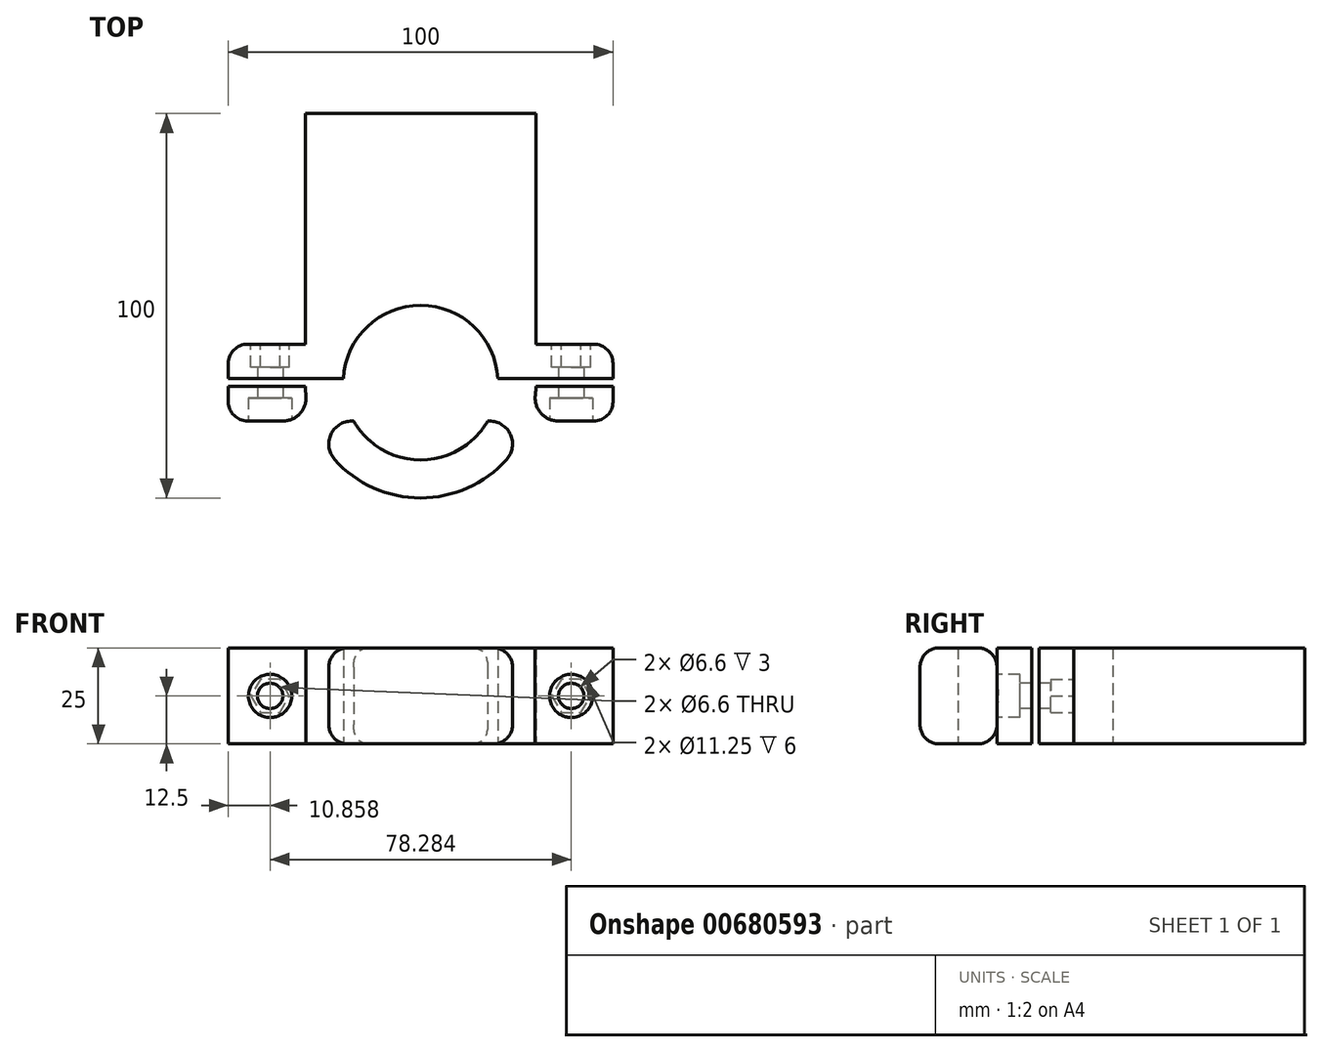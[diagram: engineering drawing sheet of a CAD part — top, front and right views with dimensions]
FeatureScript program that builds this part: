
annotation { "Feature Type Name" : "Feature", "Feature Type Description" : "" }
export const myFeature = defineFeature(function(context is Context, id is Id, definition is map)
    precondition{}
    {
        {
            var Q0;
            Q0=qCreatedBy(makeId("Top.planeOp"),FACE);
            var sketch = newSketch(context, id + "F0", { "sketchPlane" : qUnion([Q0])});
            skCircle(sketch, "E0", {"center": v(0, 0) * mm, "radius": 20.1 * mm});
            skLineSegment(sketch, "E1.bottom", {"start": v(-50, 10) * mm, "end": v(50, 10) * mm});
            skLineSegment(sketch, "E1.top", {"start": v(-50, -10) * mm, "end": v(50, -10) * mm});
            skLineSegment(sketch, "E1.left", {"start": v(-50, 10) * mm, "end": v(-50, -10) * mm});
            skLineSegment(sketch, "E1.right", {"start": v(50, 10) * mm, "end": v(50, -10) * mm});
            skLineSegment(sketch, "E2.bottom", {"start": v(-30, 0) * mm, "end": v(30, 0) * mm});
            skLineSegment(sketch, "E2.top", {"start": v(-30, 70) * mm, "end": v(30, 70) * mm});
            skLineSegment(sketch, "E2.left", {"start": v(-30, 0) * mm, "end": v(-30, 70) * mm});
            skLineSegment(sketch, "E2.right", {"start": v(30, 0) * mm, "end": v(30, 70) * mm});
            skCircle(sketch, "E3", {"center": v(0, 0) * mm, "radius": 30 * mm});
            skSolve(sketch);
        }
        {
            var Q0;
            {var subQ1=sQuery(id+"F0.wireOp",EDGE,"E2.top");Q0=makeQuery(id+"F0.imprint","IMPRINT",FACE,{"disambiguationData":[TD([[makeQuery(id+"F0.imprint","IMPRINT",EDGE,{"derivedFrom":subQ1}),-1.0]])]});}
            var Q1;
            {var subQ5=sQuery(id+"F0.wireOp",EDGE,"E1.right");Q1=makeQuery(id+"F0.imprint","IMPRINT",FACE,{"disambiguationData":[TD([[makeQuery(id+"F0.imprint","IMPRINT",EDGE,{"derivedFrom":subQ5}),-1.0]])]});}
            var Q2;
            {var subQ0=sQuery(id+"F0.wireOp",EDGE,"E1.bottom");var subQ1=sQuery(id+"F0.wireOp",EDGE,"E0");var subQ2=makeQuery(id+"F0.imprint","INTERSECT",VERTEX,{"disambiguationData":[OD(0.0)],"derivedFrom":[subQ1,subQ0]});Q2=makeQuery(id+"F0.imprint","IMPRINT",FACE,{"disambiguationData":[TD([[makeQuery(id+"F0.imprint","IMPRINT",EDGE,{"disambiguationData":[TD([[subQ2,-1.0]])],"derivedFrom":subQ1}),-1.0]])]});}
            var Q3;
            {var subQ0=sQuery(id+"F0.wireOp",EDGE,"E1.bottom");var subQ1=sQuery(id+"F0.wireOp",EDGE,"E0");var subQ2=makeQuery(id+"F0.imprint","INTERSECT",VERTEX,{"disambiguationData":[OD(1.0)],"derivedFrom":[subQ1,subQ0]});Q3=makeQuery(id+"F0.imprint","IMPRINT",FACE,{"disambiguationData":[TD([[makeQuery(id+"F0.imprint","IMPRINT",EDGE,{"disambiguationData":[TD([[subQ2,-1.0]])],"derivedFrom":subQ1}),-1.0]])]});}
            var Q4;
            {var subQ0=sQuery(id+"F0.wireOp",EDGE,"E2.bottom");var subQ1=sQuery(id+"F0.wireOp",EDGE,"E0");var subQ2=makeQuery(id+"F0.imprint","INTERSECT",VERTEX,{"disambiguationData":[OD(1.0)],"derivedFrom":[subQ1,subQ0]});Q4=makeQuery(id+"F0.imprint","IMPRINT",FACE,{"disambiguationData":[TD([[makeQuery(id+"F0.imprint","IMPRINT",EDGE,{"disambiguationData":[TD([[subQ2,-1.0]])],"derivedFrom":subQ1}),-1.0]])]});}
            var Q5;
            {var subQ0=sQuery(id+"F0.wireOp",EDGE,"E1.top");var subQ1=sQuery(id+"F0.wireOp",EDGE,"E0");var subQ2=makeQuery(id+"F0.imprint","INTERSECT",VERTEX,{"disambiguationData":[OD(0.0)],"derivedFrom":[subQ1,subQ0]});Q5=makeQuery(id+"F0.imprint","IMPRINT",FACE,{"disambiguationData":[TD([[makeQuery(id+"F0.imprint","IMPRINT",EDGE,{"disambiguationData":[TD([[subQ2,-1.0]])],"derivedFrom":subQ1}),-1.0]])]});}
            var Q6;
            {var subQ0=sQuery(id+"F0.wireOp",EDGE,"E2.bottom");var subQ1=sQuery(id+"F0.wireOp",EDGE,"E0");var subQ2=makeQuery(id+"F0.imprint","INTERSECT",VERTEX,{"disambiguationData":[OD(0.0)],"derivedFrom":[subQ1,subQ0]});Q6=makeQuery(id+"F0.imprint","IMPRINT",FACE,{"disambiguationData":[TD([[makeQuery(id+"F0.imprint","IMPRINT",EDGE,{"disambiguationData":[TD([[subQ2,1.0]])],"derivedFrom":subQ1}),-1.0]])]});}
            var Q7;
            {var subQ0=sQuery(id+"F0.wireOp",EDGE,"E1.bottom");var subQ1=sQuery(id+"F0.wireOp",EDGE,"E0");var subQ2=makeQuery(id+"F0.imprint","INTERSECT",VERTEX,{"disambiguationData":[OD(0.0)],"derivedFrom":[subQ1,subQ0]});Q7=makeQuery(id+"F0.imprint","IMPRINT",FACE,{"disambiguationData":[TD([[makeQuery(id+"F0.imprint","IMPRINT",EDGE,{"disambiguationData":[TD([[subQ2,1.0]])],"derivedFrom":subQ1}),-1.0]])]});}
            var Q8;
            {var subQ5=sQuery(id+"F0.wireOp",EDGE,"E1.left");Q8=makeQuery(id+"F0.imprint","IMPRINT",FACE,{"disambiguationData":[TD([[makeQuery(id+"F0.imprint","IMPRINT",EDGE,{"derivedFrom":subQ5}),1.0]])]});}
            var Q9;
            {var subQ0=sQuery(id+"F0.wireOp",EDGE,"E2.left");var subQ1=sQuery(id+"F0.wireOp",EDGE,"E1.bottom");var subQ2=makeQuery(id+"F0.imprint","INTERSECT",VERTEX,{"derivedFrom":[subQ1,subQ0]});Q9=makeQuery(id+"F0.imprint","IMPRINT",FACE,{"disambiguationData":[TD([[makeQuery(id+"F0.imprint","IMPRINT",EDGE,{"disambiguationData":[TD([[subQ2,-1.0]])],"derivedFrom":subQ1}),-1.0]])]});}
            var Q10;
            {var subQ0=sQuery(id+"F0.wireOp",EDGE,"E2.right");var subQ1=sQuery(id+"F0.wireOp",EDGE,"E1.bottom");var subQ2=makeQuery(id+"F0.imprint","INTERSECT",VERTEX,{"derivedFrom":[subQ1,subQ0]});Q10=makeQuery(id+"F0.imprint","IMPRINT",FACE,{"disambiguationData":[TD([[makeQuery(id+"F0.imprint","IMPRINT",EDGE,{"disambiguationData":[TD([[subQ2,1.0]])],"derivedFrom":subQ1}),-1.0]])]});}
            extrude(context, id + "F1", {"entities" : qUnion([Q0, Q1, Q2, Q3, Q4, Q5, Q6, Q7, Q8, Q9, Q10]), "depth" : 25 * mm, "offsetDistance" : 25 * mm});
        }
        {
            var Q0;
            {var subQ0=sQuery(id+"F0.wireOp",EDGE,"E1.top");Q0=makeQuery(id+"F1.opExtrude","SWEPT_FACE",FACE,{"disambiguationData":[OSD([subQ0]),TDD([makeQuery(id+"F0.imprint","IMPRINT",EDGE,{"disambiguationData":[TD([[makeQuery(id+"F0.imprint","INTERSECT",VERTEX,{"derivedFrom":[subQ0,sQuery(id+"F0.wireOp",EDGE,"E1.left")]}),-1.0]])],"derivedFrom":subQ0})])]});}
            var sketch = newSketch(context, id + "F2", { "sketchPlane" : qUnion([Q0])});
            skPoint(sketch, "E4", {"position": v(-39.14, 0) * mm});
            skPoint(sketch, "E5", {"position": v(-39.14, 12.5) * mm});
            skPoint(sketch, "E5.positionSnap0", {"position": v(-28.28, 12.5) * mm});
            skSolve(sketch);
        }
        {
            var Q0;
            {var subQ0=sQuery(id+"F0.wireOp",EDGE,"E1.top");Q0=makeQuery(id+"F1.opExtrude","SWEPT_FACE",FACE,{"disambiguationData":[OSD([subQ0]),TDD([makeQuery(id+"F0.imprint","IMPRINT",EDGE,{"disambiguationData":[TD([[makeQuery(id+"F0.imprint","INTERSECT",VERTEX,{"derivedFrom":[subQ0,sQuery(id+"F0.wireOp",EDGE,"E1.right")]}),1.0]])],"derivedFrom":subQ0})])]});}
            var sketch = newSketch(context, id + "F3", { "sketchPlane" : qUnion([Q0])});
            skPoint(sketch, "E6", {"position": v(39.14, 25) * mm});
            skPoint(sketch, "E7", {"position": v(50, 12.5) * mm});
            skPoint(sketch, "E8", {"position": v(39.14, 12.5) * mm});
            skSolve(sketch);
        }
        {
            var Q0;
            Q0=sQuery(id+"F2.wireOp",VERTEX,"E5");
            var Q1;
            Q1=sQuery(id+"F3.wireOp",VERTEX,"E8");
            var Q2;
            Q2=makeQuery(id+"F1.opExtrude","SWEPT_BODY",BODY,{"disambiguationData":[OSD([sQuery(id+"F0.wireOp",EDGE,"E0"),sQuery(id+"F0.wireOp",EDGE,"E1.bottom"),sQuery(id+"F0.wireOp",EDGE,"E1.top"),sQuery(id+"F0.wireOp",EDGE,"E1.left"),sQuery(id+"F0.wireOp",EDGE,"E1.right"),sQuery(id+"F0.wireOp",EDGE,"E2.top"),sQuery(id+"F0.wireOp",EDGE,"E2.left"),sQuery(id+"F0.wireOp",EDGE,"E2.right"),sQuery(id+"F0.wireOp",EDGE,"E3")])]});
            hole(context, id + "F4", {"style" : HoleStyle.C_BORE, "endStyle" : HoleEndStyle.THROUGH, "standardTappedOrClearance" : lookupTablePath({ "standard" : "ISO", "fit" : "Normal", "size" : "M6", "type" : "Clearance" }), "standardBlindInLast" : lookupTablePath({ "fit" : "Standard", "standard" : "ISO", "size" : "M6", "type" : "Clearance" }), "holeDiameter" : 6.6 * mm, "cBoreDiameter" : 11.25 * mm, "cBoreDepth" : 6 * mm, "majorDiameter" : 5 * mm, "isTappedThrough" : true, "tappedDepth" : 12 * mm, "tapClearance" : 3, "startFromSketch" : true, "locations" : qUnion([Q0, Q1]), "scope" : qUnion([Q2])});
        }
        {
            var Q0;
            {var subQ0=sQuery(id+"F0.wireOp",EDGE,"E1.bottom");Q0=makeQuery(id+"F1.opExtrude","SWEPT_FACE",FACE,{"disambiguationData":[OSD([subQ0]),TDD([makeQuery(id+"F0.imprint","IMPRINT",EDGE,{"disambiguationData":[TD([[makeQuery(id+"F0.imprint","INTERSECT",VERTEX,{"derivedFrom":[subQ0,sQuery(id+"F0.wireOp",EDGE,"E1.left")]}),-1.0]])],"derivedFrom":subQ0})])]});}
            var sketch = newSketch(context, id + "F5", { "sketchPlane" : qUnion([Q0])});
            skCircle(sketch, "E9.cCircle", {"center": v(39.14, 12.5) * mm, "radius": 5.05 * mm, "construction": true});
            skLineSegment(sketch, "E9.0", {"start": v(41.67, 16.87) * mm, "end": v(44.2, 12.5) * mm});
            skLineSegment(sketch, "E9.1", {"start": v(44.2, 12.5) * mm, "end": v(41.67, 8.13) * mm});
            skLineSegment(sketch, "E9.2", {"start": v(41.67, 8.13) * mm, "end": v(36.62, 8.13) * mm});
            skLineSegment(sketch, "E9.3", {"start": v(36.62, 8.13) * mm, "end": v(34.1, 12.5) * mm});
            skLineSegment(sketch, "E9.4", {"start": v(34.1, 12.5) * mm, "end": v(36.62, 16.87) * mm});
            skLineSegment(sketch, "E9.5", {"start": v(36.62, 16.87) * mm, "end": v(41.67, 16.87) * mm});
            skCircle(sketch, "E10.cCircle", {"center": v(-39.1, 12.5) * mm, "radius": 5.05 * mm, "construction": true});
            skLineSegment(sketch, "E10.0", {"start": v(-36.58, 16.87) * mm, "end": v(-34.06, 12.5) * mm});
            skLineSegment(sketch, "E10.1", {"start": v(-34.06, 12.5) * mm, "end": v(-36.58, 8.13) * mm});
            skLineSegment(sketch, "E10.2", {"start": v(-36.58, 8.13) * mm, "end": v(-41.63, 8.13) * mm});
            skLineSegment(sketch, "E10.3", {"start": v(-41.63, 8.13) * mm, "end": v(-44.16, 12.5) * mm});
            skLineSegment(sketch, "E10.4", {"start": v(-44.16, 12.5) * mm, "end": v(-41.63, 16.87) * mm});
            skLineSegment(sketch, "E10.5", {"start": v(-41.63, 16.87) * mm, "end": v(-36.58, 16.87) * mm});
            skSolve(sketch);
        }
        {
            var Q0;
            Q0=makeQuery(id+"F5.imprint","IMPRINT",FACE,{"disambiguationData":[TD([[makeQuery(id+"F5.imprint","IMPRINT",EDGE,{"derivedFrom":sQuery(id+"F5.wireOp",EDGE,"E10.0")}),-1.0]])]});
            var Q1;
            Q1=makeQuery(id+"F5.imprint","IMPRINT",FACE,{"disambiguationData":[TD([[makeQuery(id+"F5.imprint","IMPRINT",EDGE,{"derivedFrom":sQuery(id+"F5.wireOp",EDGE,"E9.0")}),-1.0]])]});
            extrude(context, id + "F6", {"entities" : qUnion([Q0, Q1]), "operationType" : NewBodyOperationType.REMOVE, "oppositeDirection" : true, "depth" : 6 * mm, "offsetDistance" : 25 * mm});
        }
        {
            var Q0;
            {var subQ0=sQuery(id+"F0.wireOp",EDGE,"E3");var subQ1=sQuery(id+"F0.wireOp",EDGE,"E1.top");Q0=makeQuery(id+"F1.opExtrude","SWEPT_EDGE",EDGE,{"disambiguationData":[OSD([subQ1,subQ0]),TDD([makeQuery(id+"F0.imprint","INTERSECT",VERTEX,{"disambiguationData":[OD(1.0)],"derivedFrom":[subQ1,subQ0]})])]});}
            var Q1;
            {var subQ0=sQuery(id+"F0.wireOp",EDGE,"E3");var subQ1=sQuery(id+"F0.wireOp",EDGE,"E1.top");Q1=makeQuery(id+"F1.opExtrude","SWEPT_EDGE",EDGE,{"disambiguationData":[OSD([subQ1,subQ0]),TDD([makeQuery(id+"F0.imprint","INTERSECT",VERTEX,{"disambiguationData":[OD(0.0)],"derivedFrom":[subQ1,subQ0]})])]});}
            fillet(context, id + "F7", {"entities" : qUnion([Q0, Q1]), "radius" : 6 * mm, "tangentPropagation" : true, "allowEdgeOverflow" : false});
        }
        {
            var Q0;
            Q0=qCreatedBy(makeId("Front.planeOp"),FACE);
            var sketch = newSketch(context, id + "F8", { "sketchPlane" : qUnion([Q0])});
            skLineSegment(sketch, "E11.bottom", {"start": v(-50, 0) * mm, "end": v(50, 0) * mm});
            skLineSegment(sketch, "E11.top", {"start": v(-50, 25) * mm, "end": v(50, 25) * mm});
            skLineSegment(sketch, "E11.left", {"start": v(-50, 0) * mm, "end": v(-50, 25) * mm});
            skLineSegment(sketch, "E11.right", {"start": v(50, 0) * mm, "end": v(50, 25) * mm});
            skSolve(sketch);
        }
        {
            var Q0;
            Q0 = qSketchRegion(id + "F8", true);
            extrude(context, id + "F9", {"entities" : qUnion([Q0]), "operationType" : NewBodyOperationType.REMOVE, "endBound" : BoundingType.SYMMETRIC, "oppositeDirection" : true, "depth" : 2 * mm, "offsetDistance" : 25 * mm});
        }
        {
            var Q0;
            Q0=makeQuery(id+"F1.opExtrude","SWEPT_FACE",FACE,{"disambiguationData":[OSD([sQuery(id+"F0.wireOp",EDGE,"E3")])]});
            fillet(context, id + "F10", {"entities" : qUnion([Q0]), "radius" : 5 * mm, "tangentPropagation" : true, "allowEdgeOverflow" : false});
        }
        {
            var Q0;
            Q0=makeQuery(id+"F1.opExtrude","SWEPT_EDGE",EDGE,{"disambiguationData":[OSD([sQuery(id+"F0.wireOp",EDGE,"E1.top"),sQuery(id+"F0.wireOp",EDGE,"E1.right")])]});
            var Q1;
            Q1=makeQuery(id+"F1.opExtrude","SWEPT_EDGE",EDGE,{"disambiguationData":[OSD([sQuery(id+"F0.wireOp",EDGE,"E1.bottom"),sQuery(id+"F0.wireOp",EDGE,"E1.right")])]});
            var Q2;
            Q2=makeQuery(id+"F1.opExtrude","SWEPT_EDGE",EDGE,{"disambiguationData":[OSD([sQuery(id+"F0.wireOp",EDGE,"E1.top"),sQuery(id+"F0.wireOp",EDGE,"E1.left")])]});
            var Q3;
            Q3=makeQuery(id+"F1.opExtrude","SWEPT_EDGE",EDGE,{"disambiguationData":[OSD([sQuery(id+"F0.wireOp",EDGE,"E1.bottom"),sQuery(id+"F0.wireOp",EDGE,"E1.left")])]});
            fillet(context, id + "F11", {"entities" : qUnion([Q0, Q1, Q2, Q3]), "radius" : 5 * mm, "tangentPropagation" : true, "allowEdgeOverflow" : false});
        }
    });
